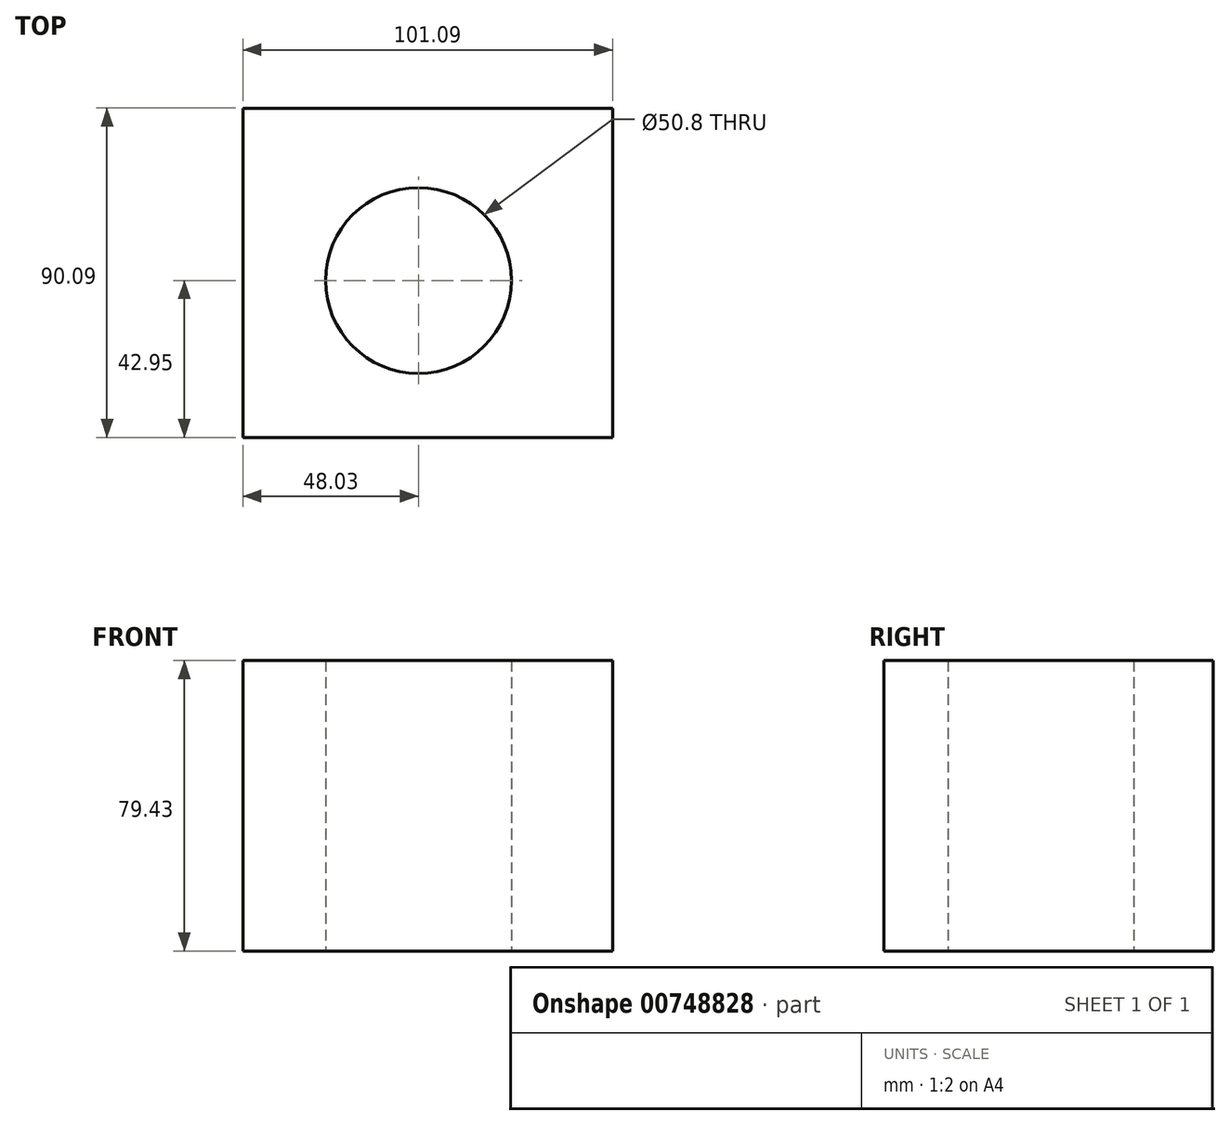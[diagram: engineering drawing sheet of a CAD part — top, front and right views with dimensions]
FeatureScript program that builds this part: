
annotation { "Feature Type Name" : "Feature", "Feature Type Description" : "" }
export const myFeature = defineFeature(function(context is Context, id is Id, definition is map)
    precondition{}
    {
        {
            var Q0;
            Q0=qCreatedBy(makeId("Top.planeOp"),FACE);
            var sketch = newSketch(context, id + "F0", { "sketchPlane" : qUnion([Q0])});
            skPoint(sketch, "E0", {"position": v(0, 0) * mm});
            skSolve(sketch);
        }
        {
            var Q0;
            Q0=qCreatedBy(makeId("Top.planeOp"),FACE);
            var sketch = newSketch(context, id + "F1", { "sketchPlane" : qUnion([Q0])});
            skLineSegment(sketch, "E1.bottom", {"start": v(-48.03, -42.95) * mm, "end": v(53.06, -42.95) * mm});
            skLineSegment(sketch, "E1.top", {"start": v(-48.03, 47.14) * mm, "end": v(53.06, 47.14) * mm});
            skLineSegment(sketch, "E1.left", {"start": v(-48.03, -42.95) * mm, "end": v(-48.03, 47.14) * mm});
            skLineSegment(sketch, "E1.right", {"start": v(53.06, -42.95) * mm, "end": v(53.06, 47.14) * mm});
            skSolve(sketch);
        }
        {
            var Q0;
            Q0=makeQuery(id+"F1.imprint","IMPRINT",FACE,{"disambiguationData":[TD([[makeQuery(id+"F1.imprint","IMPRINT",EDGE,{"derivedFrom":sQuery(id+"F1.wireOp",EDGE,"E1.bottom")}),1.0]])]});
            extrude(context, id + "F2", {"entities" : qUnion([Q0]), "depth" : 79.43 * mm, "offsetDistance" : 25.4 * mm});
        }
        {
            var Q0;
            Q0=makeQuery(id+"F2.opExtrude","CAP_FACE",FACE,{"disambiguationData":[OSD([sQuery(id+"F1.wireOp",EDGE,"E1.bottom"),sQuery(id+"F1.wireOp",EDGE,"E1.top"),sQuery(id+"F1.wireOp",EDGE,"E1.left"),sQuery(id+"F1.wireOp",EDGE,"E1.right")])],"isStart":false});
            var sketch = newSketch(context, id + "F3", { "sketchPlane" : qUnion([Q0])});
            skSolve(sketch);
        }
        {
            var Q0;
            Q0=sQuery(id+"F0.wireOp",VERTEX,"E0");
            var Q1;
            Q1=makeQuery(id+"F2.opExtrude","SWEPT_BODY",BODY,{"disambiguationData":[OSD([sQuery(id+"F1.wireOp",EDGE,"E1.bottom"),sQuery(id+"F1.wireOp",EDGE,"E1.top"),sQuery(id+"F1.wireOp",EDGE,"E1.left"),sQuery(id+"F1.wireOp",EDGE,"E1.right")])]});
            hole(context, id + "F4", {"style" : HoleStyle.SIMPLE, "endStyle" : HoleEndStyle.THROUGH, "oppositeDirection" : true, "holeDiameter" : 50.8 * mm, "majorDiameter" : 6.35 * mm, "isTappedThrough" : true, "tappedDepth" : 12.7 * mm, "tapClearance" : 3, "locations" : qUnion([Q0]), "scope" : qUnion([Q1])});
        }
    });
